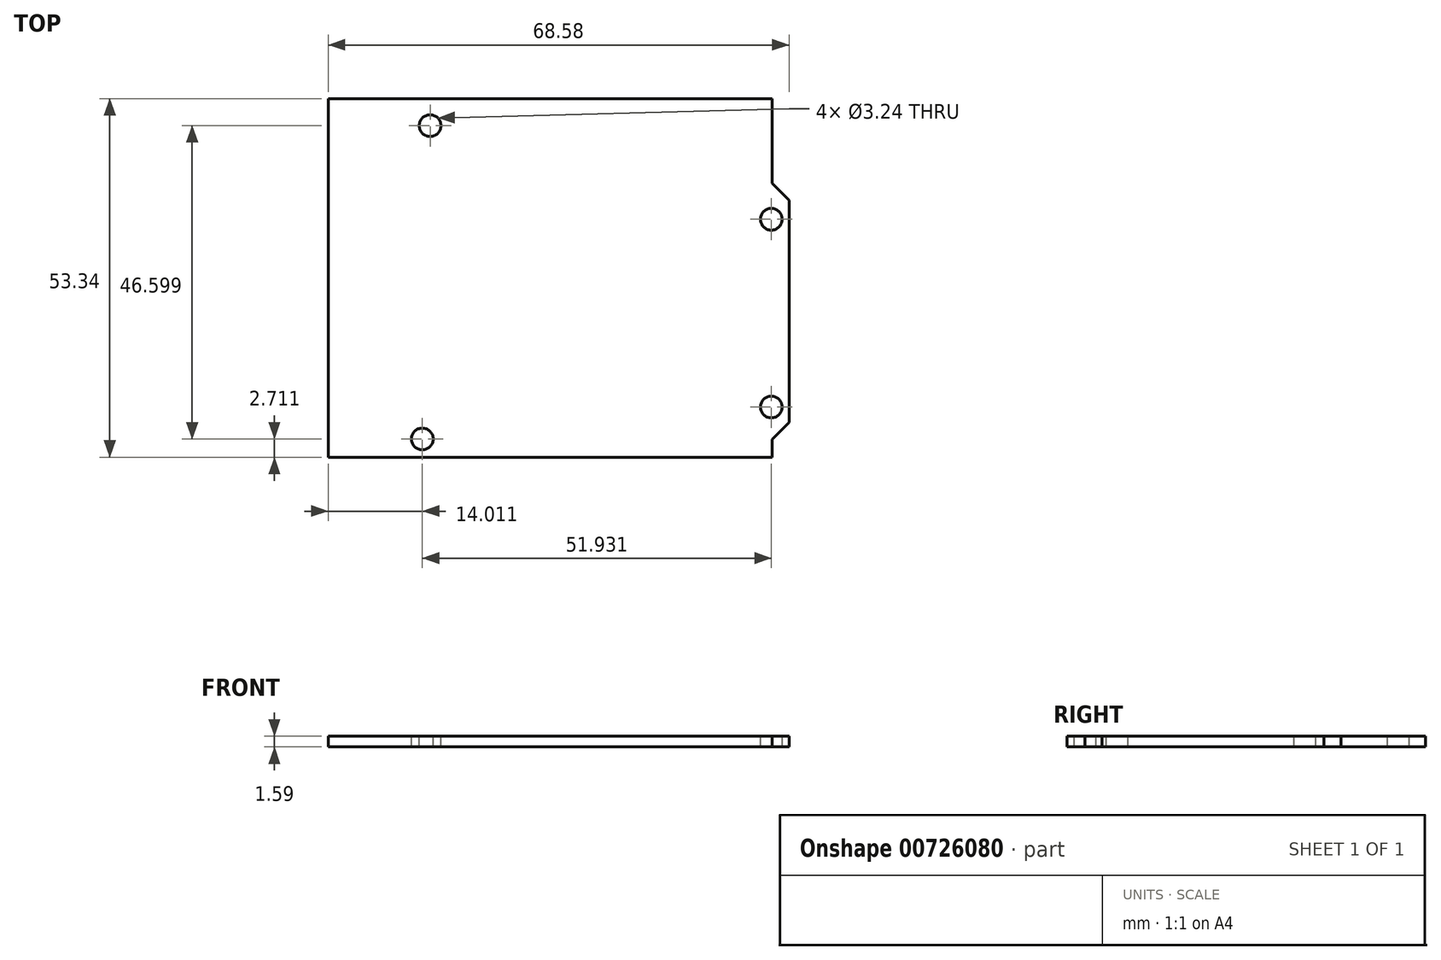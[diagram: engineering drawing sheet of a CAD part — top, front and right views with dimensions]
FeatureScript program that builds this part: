
annotation { "Feature Type Name" : "Feature", "Feature Type Description" : "" }
export const myFeature = defineFeature(function(context is Context, id is Id, definition is map)
    precondition{}
    {
        {
            var Q0;
            Q0=qCreatedBy(makeId("Top.planeOp"),FACE);
            var sketch = newSketch(context, id + "F0", { "sketchPlane" : qUnion([Q0])});
            skLineSegment(sketch, "E0", {"start": v(-34.46, 26.67) * mm, "end": v(-34.46, -26.67) * mm});
            skLineSegment(sketch, "E1", {"start": v(-34.46, -26.67) * mm, "end": v(31.58, -26.67) * mm});
            skLineSegment(sketch, "E2", {"start": v(31.58, -26.67) * mm, "end": v(31.58, 26.67) * mm});
            skLineSegment(sketch, "E3", {"start": v(31.58, 26.67) * mm, "end": v(-34.46, 26.67) * mm});
            skLineSegment(sketch, "E4", {"start": v(0, 26.67) * mm, "end": v(0, 0) * mm, "construction": true});
            skLineSegment(sketch, "E5", {"start": v(0, 0) * mm, "end": v(-34.46, 0) * mm, "construction": true});
            skLineSegment(sketch, "E6", {"start": v(31.58, -24) * mm, "end": v(34.12, -21.46) * mm});
            skLineSegment(sketch, "E7", {"start": v(34.12, -21.46) * mm, "end": v(34.12, 11.56) * mm});
            skLineSegment(sketch, "E8", {"start": v(34.12, 11.56) * mm, "end": v(31.58, 14.1) * mm});
            skSolve(sketch);
        }
        {
            var Q0;
            Q0=qSketchRegion(id+"F0",true);
            extrude(context, id + "F1", {"entities" : qUnion([Q0]), "depth" : 1.59 * mm, "offsetDistance" : 25 * mm});
        }
        {
            var Q0;
            Q0=makeQuery(id+"F1.opExtrude","CAP_FACE",FACE,{"disambiguationData":[OSD([sQuery(id+"F0.wireOp",EDGE,"E0"),sQuery(id+"F0.wireOp",EDGE,"E1"),sQuery(id+"F0.wireOp",EDGE,"E2"),sQuery(id+"F0.wireOp",EDGE,"E3"),sQuery(id+"F0.wireOp",EDGE,"E6"),sQuery(id+"F0.wireOp",EDGE,"E7"),sQuery(id+"F0.wireOp",EDGE,"E8")])],"isStart":false});
            var sketch = newSketch(context, id + "F2", { "sketchPlane" : qUnion([Q0])});
            skCircle(sketch, "E9", {"center": v(-19.29, 22.64) * mm, "radius": 1.62 * mm});
            skCircle(sketch, "E10", {"center": v(-20.45, -23.96) * mm, "radius": 1.62 * mm});
            skCircle(sketch, "E11", {"center": v(31.48, 8.72) * mm, "radius": 1.62 * mm});
            skCircle(sketch, "E12", {"center": v(31.48, -19.2) * mm, "radius": 1.62 * mm});
            skSolve(sketch);
        }
        {
            var Q0;
            Q0=qSketchRegion(id+"F2",true);
            extrude(context, id + "F3", {"entities" : qUnion([Q0]), "operationType" : NewBodyOperationType.REMOVE, "endBound" : BoundingType.THROUGH_ALL, "oppositeDirection" : true, "depth" : 25 * mm, "offsetDistance" : 25 * mm});
        }
    });
